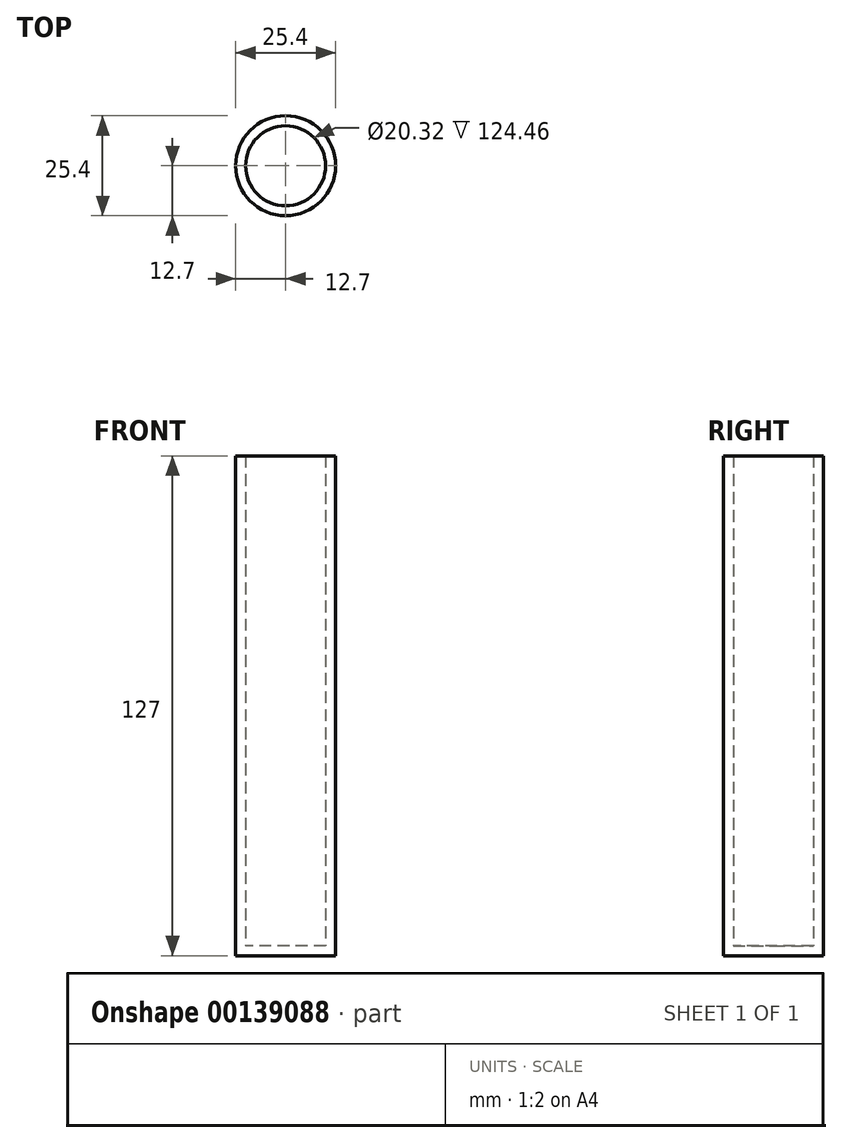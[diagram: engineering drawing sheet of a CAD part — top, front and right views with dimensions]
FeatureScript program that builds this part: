
annotation { "Feature Type Name" : "Feature", "Feature Type Description" : "" }
export const myFeature = defineFeature(function(context is Context, id is Id, definition is map)
    precondition{}
    {
        {
            var Q0;
            Q0=qCreatedBy(makeId("Top.planeOp"),FACE);
            var sketch = newSketch(context, id + "F0", { "sketchPlane" : qUnion([Q0])});
            skCircle(sketch, "E0", {"center": v(0, 0) * mm, "radius": 12.7 * mm});
            skSolve(sketch);
        }
        {
            var Q0;
            Q0 = qSketchRegion(id + "F0", true);
            extrude(context, id + "F1", {"entities" : qUnion([Q0]), "endBound" : BoundingType.SYMMETRIC, "depth" : 127 * mm});
        }
        {
            var Q0;
            Q0=makeQuery(id+"F1.opExtrude","CAP_FACE",FACE,{"disambiguationData":[OSD([sQuery(id+"F0.wireOp",EDGE,"E0")])],"isStart":false});
            shell(context, id + "F2", {"entities" : qUnion([Q0]), "thickness" : 2.54 * mm});
        }
    });
